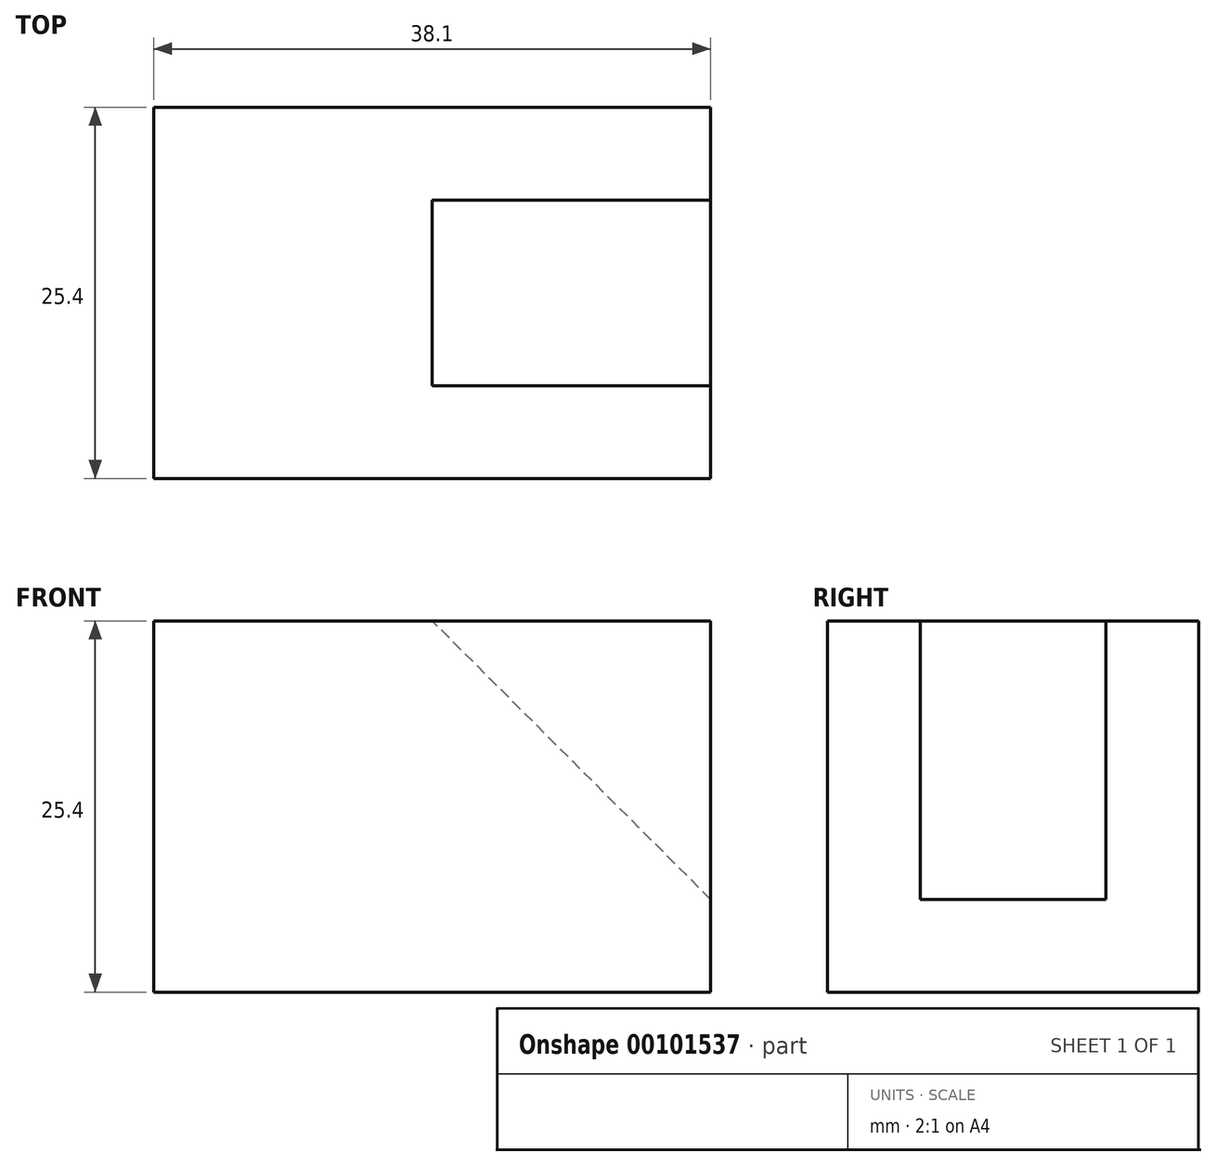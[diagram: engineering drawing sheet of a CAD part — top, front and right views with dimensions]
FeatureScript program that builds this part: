
annotation { "Feature Type Name" : "Feature", "Feature Type Description" : "" }
export const myFeature = defineFeature(function(context is Context, id is Id, definition is map)
    precondition{}
    {
        {
            var Q0;
            Q0=qCreatedBy(makeId("Front.planeOp"),FACE);
            var sketch = newSketch(context, id + "F0", { "sketchPlane" : qUnion([Q0])});
            skLineSegment(sketch, "E0", {"start": v(0, 0) * mm, "end": v(0, 25.4) * mm});
            skLineSegment(sketch, "E1", {"start": v(0, 25.4) * mm, "end": v(38.1, 25.4) * mm});
            skLineSegment(sketch, "E2", {"start": v(38.1, 25.4) * mm, "end": v(38.1, 0) * mm});
            skLineSegment(sketch, "E3", {"start": v(38.1, 0) * mm, "end": v(0, 0) * mm});
            skSolve(sketch);
        }
        {
            var Q0;
            Q0 = qSketchRegion(id + "F0", true);
            extrude(context, id + "F1", {"entities" : qUnion([Q0]), "endBound" : BoundingType.SYMMETRIC, "depth" : 25.4 * mm});
        }
        {
            var Q0;
            Q0=qCreatedBy(makeId("Front.planeOp"),FACE);
            var sketch = newSketch(context, id + "F2", { "sketchPlane" : qUnion([Q0])});
            skLineSegment(sketch, "E4", {"start": v(38.1, 25.4) * mm, "end": v(38.1, 6.35) * mm});
            skLineSegment(sketch, "E5", {"start": v(38.1, 6.35) * mm, "end": v(19.05, 25.4) * mm});
            skLineSegment(sketch, "E6", {"start": v(19.05, 25.4) * mm, "end": v(38.1, 25.4) * mm});
            skSolve(sketch);
        }
        {
            var Q0;
            Q0 = qSketchRegion(id + "F2", true);
            extrude(context, id + "F3", {"entities" : qUnion([Q0]), "operationType" : NewBodyOperationType.REMOVE, "endBound" : BoundingType.SYMMETRIC, "oppositeDirection" : true, "depth" : 12.7 * mm});
        }
    });
